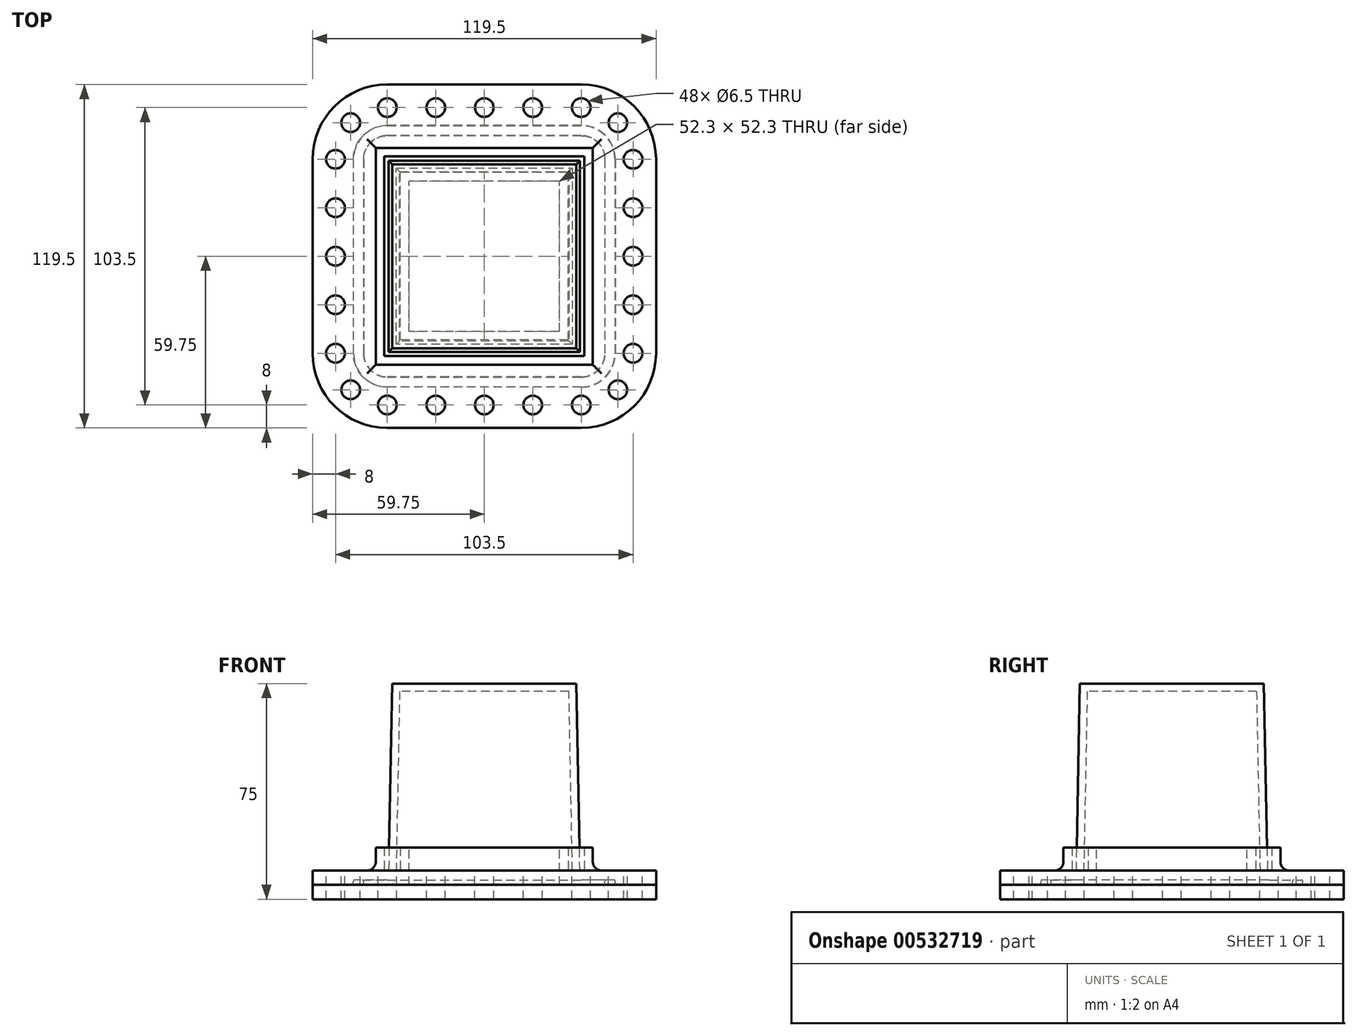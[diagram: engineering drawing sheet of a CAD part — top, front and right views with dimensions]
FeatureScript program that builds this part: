
annotation { "Feature Type Name" : "Feature", "Feature Type Description" : "" }
export const myFeature = defineFeature(function(context is Context, id is Id, definition is map)
    precondition{}
    {
        {
            var Q0;
            Q0=qCreatedBy(makeId("Top.planeOp"),FACE);
            var sketch = newSketch(context, id + "F0", { "sketchPlane" : qUnion([Q0])});
            skLineSegment(sketch, "E0.bottom", {"start": v(33.25, -33.25) * mm, "end": v(-33.25, -33.25) * mm});
            skLineSegment(sketch, "E0.top", {"start": v(33.25, 33.25) * mm, "end": v(-33.25, 33.25) * mm});
            skLineSegment(sketch, "E0.left", {"start": v(33.25, -33.25) * mm, "end": v(33.25, 33.25) * mm});
            skLineSegment(sketch, "E0.right", {"start": v(-33.25, -33.25) * mm, "end": v(-33.25, 33.25) * mm});
            skPoint(sketch, "E0.middle", {"position": v(0, 0) * mm});
            skLineSegment(sketch, "E1.0", {"start": v(-30.65, -30.65) * mm, "end": v(-30.65, 30.65) * mm});
            skLineSegment(sketch, "E1.1", {"start": v(30.65, -30.65) * mm, "end": v(-30.65, -30.65) * mm});
            skLineSegment(sketch, "E1.2", {"start": v(30.65, -30.65) * mm, "end": v(30.65, 30.65) * mm});
            skLineSegment(sketch, "E1.3", {"start": v(30.65, 30.65) * mm, "end": v(-30.65, 30.65) * mm});
            skSolve(sketch);
        }
        {
            var Q0;
            Q0=makeQuery(id+"F0.imprint","IMPRINT",FACE,{"disambiguationData":[TD([[makeQuery(id+"F0.imprint","IMPRINT",EDGE,{"derivedFrom":sQuery(id+"F0.wireOp",EDGE,"E1.0")}),-1.0]])]});
            var Q1;
            Q1=makeQuery(id+"F0.imprint","IMPRINT",FACE,{"disambiguationData":[TD([[makeQuery(id+"F0.imprint","IMPRINT",EDGE,{"derivedFrom":sQuery(id+"F0.wireOp",EDGE,"E0.bottom")}),-1.0]])]});
            extrude(context, id + "F1", {"entities" : qUnion([Q0, Q1]), "depth" : 65 * mm, "offsetDistance" : 25 * mm, "hasDraft" : true, "draftAngle" : 1.1 * degree, "draftPullDirection" : true});
        }
        {
            var Q0;
            Q0=makeQuery(id+"F1.opExtrude","CAP_FACE",FACE,{"disambiguationData":[OSD([sQuery(id+"F0.wireOp",EDGE,"E0.bottom"),sQuery(id+"F0.wireOp",EDGE,"E0.top"),sQuery(id+"F0.wireOp",EDGE,"E0.left"),sQuery(id+"F0.wireOp",EDGE,"E0.right")])],"isStart":true});
            shell(context, id + "F2", {"entities" : qUnion([Q0]), "thickness" : 2.6 * mm});
        }
        {
            var Q0;
            Q0=qCreatedBy(makeId("Top.planeOp"),FACE);
            var sketch = newSketch(context, id + "F3", { "sketchPlane" : qUnion([Q0])});
            skLineSegment(sketch, "E2.0", {"start": v(33.25, -33.25) * mm, "end": v(-33.25, -33.25) * mm, "construction": true});
            skLineSegment(sketch, "E3.0", {"start": v(-33.25, -33.25) * mm, "end": v(-33.25, 33.25) * mm, "construction": true});
            skLineSegment(sketch, "E4.0", {"start": v(33.25, 33.25) * mm, "end": v(-33.25, 33.25) * mm, "construction": true});
            skLineSegment(sketch, "E5.0", {"start": v(33.25, -33.25) * mm, "end": v(33.25, 33.25) * mm, "construction": true});
            skLineSegment(sketch, "E6.0", {"start": v(30.65, -30.65) * mm, "end": v(30.65, 30.65) * mm, "construction": true});
            skLineSegment(sketch, "E7.0", {"start": v(30.65, 30.65) * mm, "end": v(-30.65, 30.65) * mm, "construction": true});
            skLineSegment(sketch, "E8.0", {"start": v(-30.65, -30.65) * mm, "end": v(-30.65, 30.65) * mm, "construction": true});
            skLineSegment(sketch, "E9.0", {"start": v(30.65, -30.65) * mm, "end": v(-30.65, -30.65) * mm, "construction": true});
            skLineSegment(sketch, "E10.0", {"start": v(-34.75, -34.75) * mm, "end": v(-34.75, 34.75) * mm});
            skLineSegment(sketch, "E10.1", {"start": v(34.75, -34.75) * mm, "end": v(-34.75, -34.75) * mm});
            skLineSegment(sketch, "E10.2", {"start": v(34.75, -34.75) * mm, "end": v(34.75, 34.75) * mm});
            skLineSegment(sketch, "E10.3", {"start": v(34.75, 34.75) * mm, "end": v(-34.75, 34.75) * mm});
            skLineSegment(sketch, "E11.0", {"start": v(-29.15, -29.15) * mm, "end": v(-29.15, 29.15) * mm});
            skLineSegment(sketch, "E11.1", {"start": v(29.15, -29.15) * mm, "end": v(-29.15, -29.15) * mm});
            skLineSegment(sketch, "E11.2", {"start": v(29.15, -29.15) * mm, "end": v(29.15, 29.15) * mm});
            skLineSegment(sketch, "E11.3", {"start": v(29.15, 29.15) * mm, "end": v(-29.15, 29.15) * mm});
            skLineSegment(sketch, "E12.0", {"start": v(-37.75, -37.75) * mm, "end": v(-37.75, 37.75) * mm});
            skLineSegment(sketch, "E12.1", {"start": v(37.75, -37.75) * mm, "end": v(-37.75, -37.75) * mm});
            skLineSegment(sketch, "E12.2", {"start": v(37.75, -37.75) * mm, "end": v(37.75, 37.75) * mm});
            skLineSegment(sketch, "E12.3", {"start": v(37.75, 37.75) * mm, "end": v(-37.75, 37.75) * mm});
            skLineSegment(sketch, "E13.0", {"start": v(-26.15, -26.15) * mm, "end": v(-26.15, 26.15) * mm});
            skLineSegment(sketch, "E13.1", {"start": v(26.15, -26.15) * mm, "end": v(-26.15, -26.15) * mm});
            skLineSegment(sketch, "E13.2", {"start": v(26.15, -26.15) * mm, "end": v(26.15, 26.15) * mm});
            skLineSegment(sketch, "E13.3", {"start": v(26.15, 26.15) * mm, "end": v(-26.15, 26.15) * mm});
            skLineSegment(sketch, "E14.bottom", {"start": v(33.75, 43.75) * mm, "end": v(-33.75, 43.75) * mm});
            skLineSegment(sketch, "E14.top", {"start": v(33.75, -43.75) * mm, "end": v(-33.75, -43.75) * mm});
            skLineSegment(sketch, "E14.left", {"start": v(43.75, 33.75) * mm, "end": v(43.75, -33.75) * mm});
            skLineSegment(sketch, "E14.right", {"start": v(-43.75, 33.75) * mm, "end": v(-43.75, -33.75) * mm});
            skPoint(sketch, "E14.middle", {"position": v(0, 0) * mm});
            skPoint(sketch, "E15.visualSharp", {"position": v(-43.75, 43.75) * mm});
            skArc(sketch, "E15.filletArc", {"start": v(-33.75, 43.75) * mm, "mid": v(-40.82, 40.82) * mm, "end": v(-43.75, 33.75) * mm});
            skPoint(sketch, "E16.visualSharp", {"position": v(-43.75, -43.75) * mm});
            skArc(sketch, "E16.filletArc", {"start": v(-43.75, -33.75) * mm, "mid": v(-40.82, -40.82) * mm, "end": v(-33.75, -43.75) * mm});
            skPoint(sketch, "E17.visualSharp", {"position": v(43.75, -43.75) * mm});
            skArc(sketch, "E17.filletArc", {"start": v(33.75, -43.75) * mm, "mid": v(40.82, -40.82) * mm, "end": v(43.75, -33.75) * mm});
            skPoint(sketch, "E18.visualSharp", {"position": v(43.75, 43.75) * mm});
            skArc(sketch, "E18.filletArc", {"start": v(43.75, 33.75) * mm, "mid": v(40.82, 40.82) * mm, "end": v(33.75, 43.75) * mm});
            skArc(sketch, "E19.0", {"start": v(51.75, 33.75) * mm, "mid": v(46.48, 46.48) * mm, "end": v(33.75, 51.75) * mm});
            skLineSegment(sketch, "E19.1", {"start": v(51.75, 33.75) * mm, "end": v(51.75, -33.75) * mm});
            skLineSegment(sketch, "E19.2", {"start": v(33.75, 51.75) * mm, "end": v(-33.75, 51.75) * mm});
            skArc(sketch, "E19.3", {"start": v(33.75, -51.75) * mm, "mid": v(46.48, -46.48) * mm, "end": v(51.75, -33.75) * mm});
            skArc(sketch, "E19.4", {"start": v(-33.75, 51.75) * mm, "mid": v(-46.48, 46.48) * mm, "end": v(-51.75, 33.75) * mm});
            skLineSegment(sketch, "E19.5", {"start": v(-51.75, 33.75) * mm, "end": v(-51.75, -33.75) * mm});
            skArc(sketch, "E19.6", {"start": v(-51.75, -33.75) * mm, "mid": v(-46.48, -46.48) * mm, "end": v(-33.75, -51.75) * mm});
            skLineSegment(sketch, "E19.7", {"start": v(33.75, -51.75) * mm, "end": v(-33.75, -51.75) * mm});
            skArc(sketch, "E20.0", {"start": v(59.75, 33.75) * mm, "mid": v(52.13, 52.13) * mm, "end": v(33.75, 59.75) * mm});
            skLineSegment(sketch, "E20.1", {"start": v(59.75, 33.75) * mm, "end": v(59.75, -33.75) * mm});
            skLineSegment(sketch, "E20.2", {"start": v(33.75, 59.75) * mm, "end": v(-33.75, 59.75) * mm});
            skArc(sketch, "E20.3", {"start": v(33.75, -59.75) * mm, "mid": v(52.13, -52.13) * mm, "end": v(59.75, -33.75) * mm});
            skArc(sketch, "E20.4", {"start": v(-33.75, 59.75) * mm, "mid": v(-52.13, 52.13) * mm, "end": v(-59.75, 33.75) * mm});
            skLineSegment(sketch, "E20.5", {"start": v(-59.75, 33.75) * mm, "end": v(-59.75, -33.75) * mm});
            skArc(sketch, "E20.6", {"start": v(-59.75, -33.75) * mm, "mid": v(-52.13, -52.13) * mm, "end": v(-33.75, -59.75) * mm});
            skLineSegment(sketch, "E20.7", {"start": v(33.75, -59.75) * mm, "end": v(-33.75, -59.75) * mm});
            skSolve(sketch);
        }
        {
            var Q0;
            Q0=makeQuery(id+"F3.imprint","IMPRINT",FACE,{"disambiguationData":[TD([[makeQuery(id+"F3.imprint","IMPRINT",EDGE,{"derivedFrom":sQuery(id+"F3.wireOp",EDGE,"E12.0")}),1.0]])]});
            var Q1;
            Q1=makeQuery(id+"F3.imprint","IMPRINT",FACE,{"disambiguationData":[TD([[makeQuery(id+"F3.imprint","IMPRINT",EDGE,{"derivedFrom":sQuery(id+"F3.wireOp",EDGE,"E19.0")}),-1.0]])]});
            var Q2;
            Q2=makeQuery(id+"F3.imprint","IMPRINT",FACE,{"disambiguationData":[TD([[makeQuery(id+"F3.imprint","IMPRINT",EDGE,{"derivedFrom":sQuery(id+"F3.wireOp",EDGE,"E10.0")}),1.0]])]});
            var Q3;
            Q3=makeQuery(id+"F3.imprint","IMPRINT",FACE,{"disambiguationData":[TD([[makeQuery(id+"F3.imprint","IMPRINT",EDGE,{"derivedFrom":sQuery(id+"F3.wireOp",EDGE,"E10.0")}),-1.0]])]});
            var Q4;
            Q4=makeQuery(id+"F3.imprint","IMPRINT",FACE,{"disambiguationData":[TD([[makeQuery(id+"F3.imprint","IMPRINT",EDGE,{"derivedFrom":sQuery(id+"F3.wireOp",EDGE,"E11.0")}),-1.0]])]});
            var Q5;
            Q5=makeQuery(id+"F3.imprint","IMPRINT",FACE,{"disambiguationData":[TD([[makeQuery(id+"F3.imprint","IMPRINT",EDGE,{"derivedFrom":sQuery(id+"F3.wireOp",EDGE,"E14.bottom")}),-1.0]])]});
            extrude(context, id + "F4", {"entities" : qUnion([Q0, Q1, Q2, Q3, Q4, Q5]), "oppositeDirection" : true, "depth" : 5 * mm, "offsetDistance" : 25 * mm});
        }
        {
            var Q0;
            Q0=makeQuery(id+"F3.imprint","IMPRINT",FACE,{"disambiguationData":[TD([[makeQuery(id+"F3.imprint","IMPRINT",EDGE,{"derivedFrom":sQuery(id+"F3.wireOp",EDGE,"E10.0")}),1.0]])]});
            var Q1;
            Q1=makeQuery(id+"F3.imprint","IMPRINT",FACE,{"disambiguationData":[TD([[makeQuery(id+"F3.imprint","IMPRINT",EDGE,{"derivedFrom":sQuery(id+"F3.wireOp",EDGE,"E11.0")}),-1.0]])]});
            extrude(context, id + "F5", {"entities" : qUnion([Q0, Q1]), "operationType" : NewBodyOperationType.ADD, "depth" : 8 * mm, "offsetDistance" : 25 * mm});
        }
        {
            var Q0;
            Q0=qCreatedBy(makeId("Top.planeOp"),FACE);
            var sketch = newSketch(context, id + "F6", { "sketchPlane" : qUnion([Q0])});
            skArc(sketch, "E21.0", {"start": v(-33.75, 51.75) * mm, "mid": v(-46.48, 46.48) * mm, "end": v(-51.75, 33.75) * mm, "construction": true});
            skLineSegment(sketch, "E22.0", {"start": v(33.75, 51.75) * mm, "end": v(-33.75, 51.75) * mm, "construction": true});
            skArc(sketch, "E23.0", {"start": v(51.75, 33.75) * mm, "mid": v(46.48, 46.48) * mm, "end": v(33.75, 51.75) * mm, "construction": true});
            skLineSegment(sketch, "E24.0", {"start": v(51.75, 33.75) * mm, "end": v(51.75, -33.75) * mm, "construction": true});
            skPoint(sketch, "E25.0", {"position": v(46.48, -46.48) * mm});
            skLineSegment(sketch, "E26.0", {"start": v(33.75, -51.75) * mm, "end": v(-33.75, -51.75) * mm, "construction": true});
            skArc(sketch, "E27.0", {"start": v(-51.75, -33.75) * mm, "mid": v(-46.48, -46.48) * mm, "end": v(-33.75, -51.75) * mm, "construction": true});
            skLineSegment(sketch, "E28.0", {"start": v(-51.75, 33.75) * mm, "end": v(-51.75, -33.75) * mm, "construction": true});
            skArc(sketch, "E29.0", {"start": v(33.75, -51.75) * mm, "mid": v(46.48, -46.48) * mm, "end": v(51.75, -33.75) * mm, "construction": true});
            skCircle(sketch, "E30", {"center": v(0, 51.75) * mm, "radius": 3.25 * mm});
            skCircle(sketch, "E31", {"center": v(33.75, 51.75) * mm, "radius": 3.25 * mm});
            skCircle(sketch, "E32", {"center": v(51.75, 33.75) * mm, "radius": 3.25 * mm});
            skCircle(sketch, "E33", {"center": v(51.75, 0) * mm, "radius": 3.25 * mm});
            skCircle(sketch, "E34", {"center": v(51.75, -33.75) * mm, "radius": 3.25 * mm});
            skCircle(sketch, "E35", {"center": v(33.75, -51.75) * mm, "radius": 3.25 * mm});
            skCircle(sketch, "E36", {"center": v(0, -51.75) * mm, "radius": 3.25 * mm});
            skCircle(sketch, "E37", {"center": v(-33.75, -51.75) * mm, "radius": 3.25 * mm});
            skCircle(sketch, "E38", {"center": v(-51.75, -33.75) * mm, "radius": 3.25 * mm});
            skCircle(sketch, "E39", {"center": v(-51.75, 0) * mm, "radius": 3.25 * mm});
            skCircle(sketch, "E40", {"center": v(-51.75, 33.75) * mm, "radius": 3.25 * mm});
            skCircle(sketch, "E41", {"center": v(-33.75, 51.75) * mm, "radius": 3.25 * mm});
            skLineSegment(sketch, "E42", {"start": v(-33.75, 51.75) * mm, "end": v(0, 51.75) * mm, "construction": true});
            skLineSegment(sketch, "E43", {"start": v(0, 51.75) * mm, "end": v(33.75, 51.75) * mm, "construction": true});
            skLineSegment(sketch, "E44", {"start": v(51.75, 33.75) * mm, "end": v(51.75, 0) * mm, "construction": true});
            skLineSegment(sketch, "E45", {"start": v(51.75, 0) * mm, "end": v(51.75, -33.75) * mm, "construction": true});
            skLineSegment(sketch, "E46", {"start": v(33.75, -51.75) * mm, "end": v(0, -51.75) * mm, "construction": true});
            skLineSegment(sketch, "E47", {"start": v(0, -51.75) * mm, "end": v(-33.75, -51.75) * mm, "construction": true});
            skLineSegment(sketch, "E48", {"start": v(-51.75, -33.75) * mm, "end": v(-51.75, 0) * mm, "construction": true});
            skLineSegment(sketch, "E49", {"start": v(-51.75, 0) * mm, "end": v(-51.75, 33.75) * mm, "construction": true});
            skCircle(sketch, "E50", {"center": v(-51.75, 16.87) * mm, "radius": 3.25 * mm});
            skCircle(sketch, "E51", {"center": v(-46.48, 46.48) * mm, "radius": 3.25 * mm});
            skCircle(sketch, "E52", {"center": v(-16.87, 51.75) * mm, "radius": 3.25 * mm});
            skCircle(sketch, "E53", {"center": v(16.87, 51.75) * mm, "radius": 3.25 * mm});
            skCircle(sketch, "E54", {"center": v(46.48, 46.48) * mm, "radius": 3.25 * mm});
            skCircle(sketch, "E55", {"center": v(51.75, 16.87) * mm, "radius": 3.25 * mm});
            skCircle(sketch, "E56", {"center": v(51.75, -16.87) * mm, "radius": 3.25 * mm});
            skCircle(sketch, "E57", {"center": v(46.48, -46.48) * mm, "radius": 3.25 * mm});
            skCircle(sketch, "E58", {"center": v(16.87, -51.75) * mm, "radius": 3.25 * mm});
            skCircle(sketch, "E59", {"center": v(-16.87, -51.75) * mm, "radius": 3.25 * mm});
            skCircle(sketch, "E60", {"center": v(-46.48, -46.48) * mm, "radius": 3.25 * mm});
            skCircle(sketch, "E61", {"center": v(-51.75, -16.87) * mm, "radius": 3.25 * mm});
            skSolve(sketch);
        }
        {
            var Q0;
            Q0=makeQuery(id+"F6.imprint","IMPRINT",FACE,{"disambiguationData":[TD([[makeQuery(id+"F6.imprint","IMPRINT",EDGE,{"derivedFrom":sQuery(id+"F6.wireOp",EDGE,"E51")}),1.0]])]});
            var Q1;
            Q1=makeQuery(id+"F6.imprint","IMPRINT",FACE,{"disambiguationData":[TD([[makeQuery(id+"F6.imprint","IMPRINT",EDGE,{"derivedFrom":sQuery(id+"F6.wireOp",EDGE,"E41")}),1.0]])]});
            var Q2;
            Q2=makeQuery(id+"F6.imprint","IMPRINT",FACE,{"disambiguationData":[TD([[makeQuery(id+"F6.imprint","IMPRINT",EDGE,{"derivedFrom":sQuery(id+"F6.wireOp",EDGE,"E52")}),1.0]])]});
            var Q3;
            Q3=makeQuery(id+"F6.imprint","IMPRINT",FACE,{"disambiguationData":[TD([[makeQuery(id+"F6.imprint","IMPRINT",EDGE,{"derivedFrom":sQuery(id+"F6.wireOp",EDGE,"E30")}),1.0]])]});
            var Q4;
            Q4=makeQuery(id+"F6.imprint","IMPRINT",FACE,{"disambiguationData":[TD([[makeQuery(id+"F6.imprint","IMPRINT",EDGE,{"derivedFrom":sQuery(id+"F6.wireOp",EDGE,"E53")}),1.0]])]});
            var Q5;
            Q5=makeQuery(id+"F6.imprint","IMPRINT",FACE,{"disambiguationData":[TD([[makeQuery(id+"F6.imprint","IMPRINT",EDGE,{"derivedFrom":sQuery(id+"F6.wireOp",EDGE,"E54")}),1.0]])]});
            var Q6;
            Q6=makeQuery(id+"F6.imprint","IMPRINT",FACE,{"disambiguationData":[TD([[makeQuery(id+"F6.imprint","IMPRINT",EDGE,{"derivedFrom":sQuery(id+"F6.wireOp",EDGE,"E31")}),1.0]])]});
            var Q7;
            Q7=makeQuery(id+"F6.imprint","IMPRINT",FACE,{"disambiguationData":[TD([[makeQuery(id+"F6.imprint","IMPRINT",EDGE,{"derivedFrom":sQuery(id+"F6.wireOp",EDGE,"E32")}),1.0]])]});
            var Q8;
            Q8=makeQuery(id+"F6.imprint","IMPRINT",FACE,{"disambiguationData":[TD([[makeQuery(id+"F6.imprint","IMPRINT",EDGE,{"derivedFrom":sQuery(id+"F6.wireOp",EDGE,"E55")}),1.0]])]});
            var Q9;
            Q9=makeQuery(id+"F6.imprint","IMPRINT",FACE,{"disambiguationData":[TD([[makeQuery(id+"F6.imprint","IMPRINT",EDGE,{"derivedFrom":sQuery(id+"F6.wireOp",EDGE,"E33")}),1.0]])]});
            var Q10;
            Q10=makeQuery(id+"F6.imprint","IMPRINT",FACE,{"disambiguationData":[TD([[makeQuery(id+"F6.imprint","IMPRINT",EDGE,{"derivedFrom":sQuery(id+"F6.wireOp",EDGE,"E56")}),1.0]])]});
            var Q11;
            Q11=makeQuery(id+"F6.imprint","IMPRINT",FACE,{"disambiguationData":[TD([[makeQuery(id+"F6.imprint","IMPRINT",EDGE,{"derivedFrom":sQuery(id+"F6.wireOp",EDGE,"E35")}),1.0]])]});
            var Q12;
            Q12=makeQuery(id+"F6.imprint","IMPRINT",FACE,{"disambiguationData":[TD([[makeQuery(id+"F6.imprint","IMPRINT",EDGE,{"derivedFrom":sQuery(id+"F6.wireOp",EDGE,"E57")}),1.0]])]});
            var Q13;
            Q13=makeQuery(id+"F6.imprint","IMPRINT",FACE,{"disambiguationData":[TD([[makeQuery(id+"F6.imprint","IMPRINT",EDGE,{"derivedFrom":sQuery(id+"F6.wireOp",EDGE,"E34")}),1.0]])]});
            var Q14;
            Q14=makeQuery(id+"F6.imprint","IMPRINT",FACE,{"disambiguationData":[TD([[makeQuery(id+"F6.imprint","IMPRINT",EDGE,{"derivedFrom":sQuery(id+"F6.wireOp",EDGE,"E58")}),1.0]])]});
            var Q15;
            Q15=makeQuery(id+"F6.imprint","IMPRINT",FACE,{"disambiguationData":[TD([[makeQuery(id+"F6.imprint","IMPRINT",EDGE,{"derivedFrom":sQuery(id+"F6.wireOp",EDGE,"E36")}),1.0]])]});
            var Q16;
            Q16=makeQuery(id+"F6.imprint","IMPRINT",FACE,{"disambiguationData":[TD([[makeQuery(id+"F6.imprint","IMPRINT",EDGE,{"derivedFrom":sQuery(id+"F6.wireOp",EDGE,"E59")}),1.0]])]});
            var Q17;
            Q17=makeQuery(id+"F6.imprint","IMPRINT",FACE,{"disambiguationData":[TD([[makeQuery(id+"F6.imprint","IMPRINT",EDGE,{"derivedFrom":sQuery(id+"F6.wireOp",EDGE,"E37")}),1.0]])]});
            var Q18;
            Q18=makeQuery(id+"F6.imprint","IMPRINT",FACE,{"disambiguationData":[TD([[makeQuery(id+"F6.imprint","IMPRINT",EDGE,{"derivedFrom":sQuery(id+"F6.wireOp",EDGE,"E60")}),1.0]])]});
            var Q19;
            Q19=makeQuery(id+"F6.imprint","IMPRINT",FACE,{"disambiguationData":[TD([[makeQuery(id+"F6.imprint","IMPRINT",EDGE,{"derivedFrom":sQuery(id+"F6.wireOp",EDGE,"E38")}),1.0]])]});
            var Q20;
            Q20=makeQuery(id+"F6.imprint","IMPRINT",FACE,{"disambiguationData":[TD([[makeQuery(id+"F6.imprint","IMPRINT",EDGE,{"derivedFrom":sQuery(id+"F6.wireOp",EDGE,"E61")}),1.0]])]});
            var Q21;
            Q21=makeQuery(id+"F6.imprint","IMPRINT",FACE,{"disambiguationData":[TD([[makeQuery(id+"F6.imprint","IMPRINT",EDGE,{"derivedFrom":sQuery(id+"F6.wireOp",EDGE,"E39")}),1.0]])]});
            var Q22;
            Q22=makeQuery(id+"F6.imprint","IMPRINT",FACE,{"disambiguationData":[TD([[makeQuery(id+"F6.imprint","IMPRINT",EDGE,{"derivedFrom":sQuery(id+"F6.wireOp",EDGE,"E50")}),1.0]])]});
            var Q23;
            Q23=makeQuery(id+"F6.imprint","IMPRINT",FACE,{"disambiguationData":[TD([[makeQuery(id+"F6.imprint","IMPRINT",EDGE,{"derivedFrom":sQuery(id+"F6.wireOp",EDGE,"E40")}),1.0]])]});
            var Q24;
            Q24=sQuery(id+"F6.wireOp",EDGE,"E51");
            var Q25;
            Q25=sQuery(id+"F6.wireOp",EDGE,"E41");
            var Q26;
            Q26=sQuery(id+"F6.wireOp",EDGE,"E52");
            var Q27;
            Q27=sQuery(id+"F6.wireOp",EDGE,"E30");
            var Q28;
            Q28=sQuery(id+"F6.wireOp",EDGE,"E53");
            var Q29;
            Q29=sQuery(id+"F6.wireOp",EDGE,"E31");
            var Q30;
            Q30=sQuery(id+"F6.wireOp",EDGE,"E54");
            var Q31;
            Q31=sQuery(id+"F6.wireOp",EDGE,"E32");
            var Q32;
            Q32=sQuery(id+"F6.wireOp",EDGE,"E55");
            var Q33;
            Q33=sQuery(id+"F6.wireOp",EDGE,"E33");
            var Q34;
            Q34=sQuery(id+"F6.wireOp",EDGE,"E56");
            var Q35;
            Q35=sQuery(id+"F6.wireOp",EDGE,"E34");
            var Q36;
            Q36=sQuery(id+"F6.wireOp",EDGE,"E57");
            var Q37;
            Q37=sQuery(id+"F6.wireOp",EDGE,"E35");
            var Q38;
            Q38=sQuery(id+"F6.wireOp",EDGE,"E58");
            var Q39;
            Q39=sQuery(id+"F6.wireOp",EDGE,"E36");
            var Q40;
            Q40=sQuery(id+"F6.wireOp",EDGE,"E59");
            var Q41;
            Q41=sQuery(id+"F6.wireOp",EDGE,"E37");
            var Q42;
            Q42=sQuery(id+"F6.wireOp",EDGE,"E60");
            var Q43;
            Q43=sQuery(id+"F6.wireOp",EDGE,"E38");
            var Q44;
            Q44=sQuery(id+"F6.wireOp",EDGE,"E61");
            var Q45;
            Q45=sQuery(id+"F6.wireOp",EDGE,"E39");
            var Q46;
            Q46=sQuery(id+"F6.wireOp",EDGE,"E50");
            var Q47;
            Q47=sQuery(id+"F6.wireOp",EDGE,"E40");
            extrude(context, id + "F7", {"entities" : qUnion([Q0, Q1, Q2, Q3, Q4, Q5, Q6, Q7, Q8, Q9, Q10, Q11, Q12, Q13, Q14, Q15, Q16, Q17, Q18, Q19, Q20, Q21, Q22, Q23]), "operationType" : NewBodyOperationType.REMOVE, "surfaceEntities" : qUnion([Q24, Q25, Q26, Q27, Q28, Q29, Q30, Q31, Q32, Q33, Q34, Q35, Q36, Q37, Q38, Q39, Q40, Q41, Q42, Q43, Q44, Q45, Q46, Q47]), "oppositeDirection" : true, "depth" : 25 * mm, "offsetDistance" : 25 * mm});
        }
        {
            var Q0;
            Q0=makeQuery(id+"F4.opExtrude","CAP_FACE",FACE,{"disambiguationData":[OSD([sQuery(id+"F3.wireOp",EDGE,"E13.0"),sQuery(id+"F3.wireOp",EDGE,"E13.1"),sQuery(id+"F3.wireOp",EDGE,"E13.2"),sQuery(id+"F3.wireOp",EDGE,"E13.3"),sQuery(id+"F3.wireOp",EDGE,"E20.0"),sQuery(id+"F3.wireOp",EDGE,"E20.1"),sQuery(id+"F3.wireOp",EDGE,"E20.2"),sQuery(id+"F3.wireOp",EDGE,"E20.3"),sQuery(id+"F3.wireOp",EDGE,"E20.4"),sQuery(id+"F3.wireOp",EDGE,"E20.5"),sQuery(id+"F3.wireOp",EDGE,"E20.6"),sQuery(id+"F3.wireOp",EDGE,"E20.7")])],"isStart":false});
            var sketch = newSketch(context, id + "F8", { "sketchPlane" : qUnion([Q0])});
            skLineSegment(sketch, "E62.0.0", {"start": v(33.75, 59.75) * mm, "end": v(-33.75, 59.75) * mm});
            skArc(sketch, "E62.0.1", {"start": v(-33.75, 59.75) * mm, "mid": v(-52.13, 52.13) * mm, "end": v(-59.75, 33.75) * mm});
            skLineSegment(sketch, "E62.0.2", {"start": v(-59.75, 33.75) * mm, "end": v(-59.75, -33.75) * mm});
            skArc(sketch, "E62.0.3", {"start": v(-59.75, -33.75) * mm, "mid": v(-52.13, -52.13) * mm, "end": v(-33.75, -59.75) * mm});
            skLineSegment(sketch, "E62.0.4", {"start": v(-33.75, -59.75) * mm, "end": v(33.75, -59.75) * mm});
            skArc(sketch, "E62.0.5", {"start": v(33.75, -59.75) * mm, "mid": v(52.13, -52.13) * mm, "end": v(59.75, -33.75) * mm});
            skLineSegment(sketch, "E62.0.6", {"start": v(59.75, -33.75) * mm, "end": v(59.75, 33.75) * mm});
            skArc(sketch, "E62.0.7", {"start": v(59.75, 33.75) * mm, "mid": v(52.13, 52.13) * mm, "end": v(33.75, 59.75) * mm});
            skCircle(sketch, "E63.0", {"center": v(-46.48, 46.48) * mm, "radius": 3.25 * mm});
            skCircle(sketch, "E64.0", {"center": v(-33.75, 51.75) * mm, "radius": 3.25 * mm});
            skCircle(sketch, "E65.0", {"center": v(-16.87, 51.75) * mm, "radius": 3.25 * mm});
            skCircle(sketch, "E66.0", {"center": v(0, 51.75) * mm, "radius": 3.25 * mm});
            skCircle(sketch, "E67.0", {"center": v(16.87, 51.75) * mm, "radius": 3.25 * mm});
            skCircle(sketch, "E68.0", {"center": v(33.75, 51.75) * mm, "radius": 3.25 * mm});
            skCircle(sketch, "E69.0", {"center": v(46.48, 46.48) * mm, "radius": 3.25 * mm});
            skCircle(sketch, "E70.0", {"center": v(51.75, 33.75) * mm, "radius": 3.25 * mm});
            skCircle(sketch, "E70.1", {"center": v(51.75, 16.87) * mm, "radius": 3.25 * mm});
            skCircle(sketch, "E70.2", {"center": v(51.75, 0) * mm, "radius": 3.25 * mm});
            skCircle(sketch, "E70.3", {"center": v(51.75, -16.87) * mm, "radius": 3.25 * mm});
            skCircle(sketch, "E70.4", {"center": v(51.75, -33.75) * mm, "radius": 3.25 * mm});
            skCircle(sketch, "E70.5", {"center": v(46.48, -46.48) * mm, "radius": 3.25 * mm});
            skCircle(sketch, "E70.6", {"center": v(33.75, -51.75) * mm, "radius": 3.25 * mm});
            skCircle(sketch, "E70.7", {"center": v(16.87, -51.75) * mm, "radius": 3.25 * mm});
            skCircle(sketch, "E70.8", {"center": v(0, -51.75) * mm, "radius": 3.25 * mm});
            skCircle(sketch, "E70.9", {"center": v(-16.87, -51.75) * mm, "radius": 3.25 * mm});
            skCircle(sketch, "E70.10", {"center": v(-33.75, -51.75) * mm, "radius": 3.25 * mm});
            skCircle(sketch, "E70.11", {"center": v(-46.48, -46.48) * mm, "radius": 3.25 * mm});
            skCircle(sketch, "E70.12", {"center": v(-51.75, -33.75) * mm, "radius": 3.25 * mm});
            skCircle(sketch, "E70.13", {"center": v(-51.75, -16.87) * mm, "radius": 3.25 * mm});
            skCircle(sketch, "E70.14", {"center": v(-51.75, 0) * mm, "radius": 3.25 * mm});
            skCircle(sketch, "E70.15", {"center": v(-51.75, 16.87) * mm, "radius": 3.25 * mm});
            skCircle(sketch, "E70.16", {"center": v(-51.75, 33.75) * mm, "radius": 3.25 * mm});
            skSolve(sketch);
        }
        {
            var Q0;
            Q0 = qSketchRegion(id + "F8", true);
            extrude(context, id + "F9", {"entities" : qUnion([Q0]), "depth" : 5 * mm, "offsetDistance" : 25 * mm});
        }
        {
            var Q0;
            Q0=makeQuery(id+"F4.opExtrude","CAP_FACE",FACE,{"disambiguationData":[OSD([sQuery(id+"F3.wireOp",EDGE,"E13.0"),sQuery(id+"F3.wireOp",EDGE,"E13.1"),sQuery(id+"F3.wireOp",EDGE,"E13.2"),sQuery(id+"F3.wireOp",EDGE,"E13.3"),sQuery(id+"F3.wireOp",EDGE,"E20.0"),sQuery(id+"F3.wireOp",EDGE,"E20.1"),sQuery(id+"F3.wireOp",EDGE,"E20.2"),sQuery(id+"F3.wireOp",EDGE,"E20.3"),sQuery(id+"F3.wireOp",EDGE,"E20.4"),sQuery(id+"F3.wireOp",EDGE,"E20.5"),sQuery(id+"F3.wireOp",EDGE,"E20.6"),sQuery(id+"F3.wireOp",EDGE,"E20.7")])],"isStart":false});
            var sketch = newSketch(context, id + "F10", { "sketchPlane" : qUnion([Q0])});
            skLineSegment(sketch, "E71.0", {"start": v(-43.75, -33.75) * mm, "end": v(-43.75, 33.75) * mm, "construction": true});
            skArc(sketch, "E72.0", {"start": v(-33.75, -43.75) * mm, "mid": v(-40.82, -40.82) * mm, "end": v(-43.75, -33.75) * mm, "construction": true});
            skLineSegment(sketch, "E73.0", {"start": v(33.75, -43.75) * mm, "end": v(-33.75, -43.75) * mm, "construction": true});
            skArc(sketch, "E74.0", {"start": v(43.75, -33.75) * mm, "mid": v(40.82, -40.82) * mm, "end": v(33.75, -43.75) * mm, "construction": true});
            skLineSegment(sketch, "E75.0", {"start": v(43.75, -33.75) * mm, "end": v(43.75, 33.75) * mm, "construction": true});
            skArc(sketch, "E76.0", {"start": v(-43.75, 33.75) * mm, "mid": v(-40.82, 40.82) * mm, "end": v(-33.75, 43.75) * mm, "construction": true});
            skLineSegment(sketch, "E77.0", {"start": v(33.75, 43.75) * mm, "end": v(-33.75, 43.75) * mm, "construction": true});
            skArc(sketch, "E78.0", {"start": v(33.75, 43.75) * mm, "mid": v(40.82, 40.82) * mm, "end": v(43.75, 33.75) * mm, "construction": true});
            skLineSegment(sketch, "E79.0", {"start": v(-45.45, -33.75) * mm, "end": v(-45.45, 33.75) * mm});
            skArc(sketch, "E79.1", {"start": v(-33.75, -45.45) * mm, "mid": v(-42.02, -42.02) * mm, "end": v(-45.45, -33.75) * mm});
            skArc(sketch, "E79.2", {"start": v(-45.45, 33.75) * mm, "mid": v(-42.02, 42.02) * mm, "end": v(-33.75, 45.45) * mm});
            skLineSegment(sketch, "E79.3", {"start": v(33.75, -45.45) * mm, "end": v(-33.75, -45.45) * mm});
            skLineSegment(sketch, "E79.4", {"start": v(33.75, 45.45) * mm, "end": v(-33.75, 45.45) * mm});
            skArc(sketch, "E79.5", {"start": v(33.75, 45.45) * mm, "mid": v(42.02, 42.02) * mm, "end": v(45.45, 33.75) * mm});
            skLineSegment(sketch, "E79.6", {"start": v(45.45, -33.75) * mm, "end": v(45.45, 33.75) * mm});
            skArc(sketch, "E79.7", {"start": v(45.45, -33.75) * mm, "mid": v(42.02, -42.02) * mm, "end": v(33.75, -45.45) * mm});
            skArc(sketch, "E80.0", {"start": v(-33.75, -42.05) * mm, "mid": v(-39.62, -39.62) * mm, "end": v(-42.05, -33.75) * mm});
            skLineSegment(sketch, "E80.1", {"start": v(33.75, -42.05) * mm, "end": v(-33.75, -42.05) * mm});
            skLineSegment(sketch, "E80.2", {"start": v(-42.05, -33.75) * mm, "end": v(-42.05, 33.75) * mm});
            skArc(sketch, "E80.3", {"start": v(42.05, -33.75) * mm, "mid": v(39.62, -39.62) * mm, "end": v(33.75, -42.05) * mm});
            skArc(sketch, "E80.4", {"start": v(-42.05, 33.75) * mm, "mid": v(-39.62, 39.62) * mm, "end": v(-33.75, 42.05) * mm});
            skLineSegment(sketch, "E80.5", {"start": v(33.75, 42.05) * mm, "end": v(-33.75, 42.05) * mm});
            skArc(sketch, "E80.6", {"start": v(33.75, 42.05) * mm, "mid": v(39.62, 39.62) * mm, "end": v(42.05, 33.75) * mm});
            skLineSegment(sketch, "E80.7", {"start": v(42.05, -33.75) * mm, "end": v(42.05, 33.75) * mm});
            skSolve(sketch);
        }
        {
            var Q0;
            Q0=makeQuery(id+"F10.imprint","IMPRINT",FACE,{"disambiguationData":[TD([[makeQuery(id+"F10.imprint","IMPRINT",EDGE,{"derivedFrom":sQuery(id+"F10.wireOp",EDGE,"E79.0")}),-1.0]])]});
            extrude(context, id + "F11", {"entities" : qUnion([Q0]), "operationType" : NewBodyOperationType.REMOVE, "oppositeDirection" : true, "depth" : 1.7 * mm, "offsetDistance" : 25 * mm, "hasDraft" : true, "draftAngle" : 5 * degree});
        }
        {
            var Q0;
            Q0=makeQuery(id+"F11.boolean.opBoolean","COPY",EDGE,{"derivedFrom":makeQuery(id+"F11.opExtrude","CAP_EDGE",EDGE,{"disambiguationData":[OSD([sQuery(id+"F10.wireOp",EDGE,"E79.2")])],"isStart":false})});
            var Q1;
            Q1=makeQuery(id+"F11.boolean.opBoolean","COPY",FACE,{"derivedFrom":makeQuery(id+"F11.opExtrude","CAP_FACE",FACE,{"disambiguationData":[OSD([sQuery(id+"F10.wireOp",EDGE,"7c0de443-8626-4496-b011-e60e08350350.0"),sQuery(id+"F10.wireOp",EDGE,"7c0de443-8626-4496-b011-e60e08350350.1"),sQuery(id+"F10.wireOp",EDGE,"7c0de443-8626-4496-b011-e60e08350350.2"),sQuery(id+"F10.wireOp",EDGE,"7c0de443-8626-4496-b011-e60e08350350.3"),sQuery(id+"F10.wireOp",EDGE,"7c0de443-8626-4496-b011-e60e08350350.4"),sQuery(id+"F10.wireOp",EDGE,"7c0de443-8626-4496-b011-e60e08350350.5"),sQuery(id+"F10.wireOp",EDGE,"7c0de443-8626-4496-b011-e60e08350350.6"),sQuery(id+"F10.wireOp",EDGE,"7c0de443-8626-4496-b011-e60e08350350.7"),sQuery(id+"F10.wireOp",EDGE,"E79.0"),sQuery(id+"F10.wireOp",EDGE,"E79.1"),sQuery(id+"F10.wireOp",EDGE,"E79.2"),sQuery(id+"F10.wireOp",EDGE,"E79.3"),sQuery(id+"F10.wireOp",EDGE,"E79.4"),sQuery(id+"F10.wireOp",EDGE,"E79.5"),sQuery(id+"F10.wireOp",EDGE,"E79.6"),sQuery(id+"F10.wireOp",EDGE,"E79.7")])],"isStart":false})});
            fillet(context, id + "F12", {"entities" : qUnion([Q0, Q1]), "radius" : 0.5 * mm, "tangentPropagation" : true, "allowEdgeOverflow" : false});
        }
        {
            var Q0;
            Q0=makeQuery(id+"F5.opExtrude","CAP_EDGE",EDGE,{"disambiguationData":[OSD([sQuery(id+"F3.wireOp",EDGE,"E12.0")])],"isStart":true});
            var Q1;
            Q1=makeQuery(id+"F5.opExtrude","CAP_EDGE",EDGE,{"disambiguationData":[OSD([sQuery(id+"F3.wireOp",EDGE,"E12.1")])],"isStart":true});
            var Q2;
            Q2=makeQuery(id+"F5.opExtrude","CAP_EDGE",EDGE,{"disambiguationData":[OSD([sQuery(id+"F3.wireOp",EDGE,"E12.2")])],"isStart":true});
            var Q3;
            Q3=makeQuery(id+"F5.opExtrude","CAP_EDGE",EDGE,{"disambiguationData":[OSD([sQuery(id+"F3.wireOp",EDGE,"E12.3")])],"isStart":true});
            fillet(context, id + "F13", {"entities" : qUnion([Q0, Q1, Q2, Q3]), "radius" : 3 * mm, "tangentPropagation" : true, "allowEdgeOverflow" : false});
        }
    });
